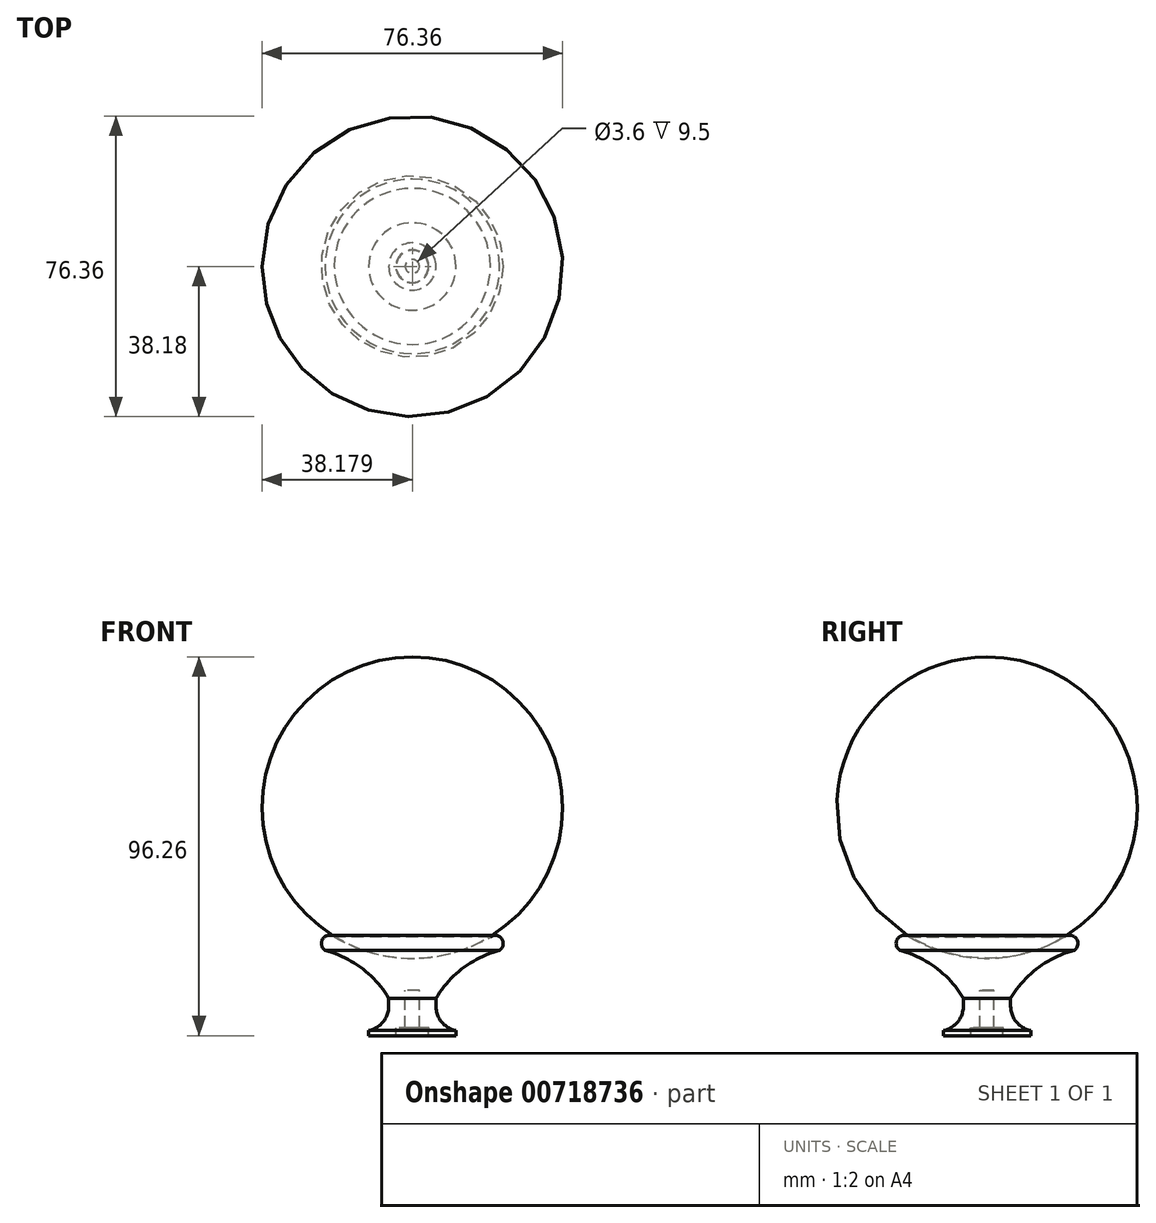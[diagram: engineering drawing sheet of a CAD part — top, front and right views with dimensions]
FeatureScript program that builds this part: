
annotation { "Feature Type Name" : "Feature", "Feature Type Description" : "" }
export const myFeature = defineFeature(function(context is Context, id is Id, definition is map)
    precondition{}
    {
        {
            var Q0;
            Q0=qCreatedBy(makeId("Front.planeOp"),FACE);
            var sketch = newSketch(context, id + "F0", { "sketchPlane" : qUnion([Q0])});
            skLineSegment(sketch, "E0", {"start": v(1.99, 51.39) * mm, "end": v(1.99, 43.23) * mm});
            skLineSegment(sketch, "E1", {"start": v(1.99, 43.23) * mm, "end": v(0.19, 43.23) * mm});
            skLineSegment(sketch, "E2", {"start": v(0.19, 43.23) * mm, "end": v(0.19, 33.73) * mm});
            skLineSegment(sketch, "E3", {"start": v(0.19, 33.73) * mm, "end": v(-2.2, 33.73) * mm});
            skLineSegment(sketch, "E4", {"start": v(-2.2, 33.73) * mm, "end": v(-2.11, 31.73) * mm});
            skLineSegment(sketch, "E5", {"start": v(-2.11, 31.73) * mm, "end": v(-9.11, 31.73) * mm});
            skLineSegment(sketch, "E6", {"start": v(-9.11, 31.73) * mm, "end": v(-9.11, 33.03) * mm});
            skArc(sketch, "E7", {"start": v(-17.84, 56.85) * mm, "mid": v(-20.75, 56.33) * mm, "end": v(-20.18, 53.43) * mm});
            skArc(sketch, "E8", {"start": v(-17.84, 56.85) * mm, "mid": v(-8.3, 52.76) * mm, "end": v(1.99, 51.39) * mm});
            skLineSegment(sketch, "E9", {"start": v(-4.01, 41.23) * mm, "end": v(-4.01, 39.23) * mm});
            skArc(sketch, "E10", {"start": v(-4.01, 41.23) * mm, "mid": v(-10.9, 48.91) * mm, "end": v(-20.18, 53.43) * mm});
            skArc(sketch, "E11", {"start": v(-9.11, 33.03) * mm, "mid": v(-5.45, 35.22) * mm, "end": v(-4.01, 39.23) * mm});
            skSolve(sketch);
        }
        {
            var Q0;
            Q0=makeQuery(id+"F0.imprint","IMPRINT",FACE,{"disambiguationData":[TD([[makeQuery(id+"F0.imprint","IMPRINT",EDGE,{"derivedFrom":sQuery(id+"F0.wireOp",EDGE,"E0")}),-1.0]])]});
            var Q1;
            Q1=sQuery(id+"F0.wireOp",EDGE,"E0");
            revolve(context, id + "F1", {"surfaceOperationType" : NewSurfaceOperationType.NEW, "entities" : qUnion([Q0]), "axis" : qUnion([Q1]), "revolveType" : RevolveType.FULL});
        }
    });
